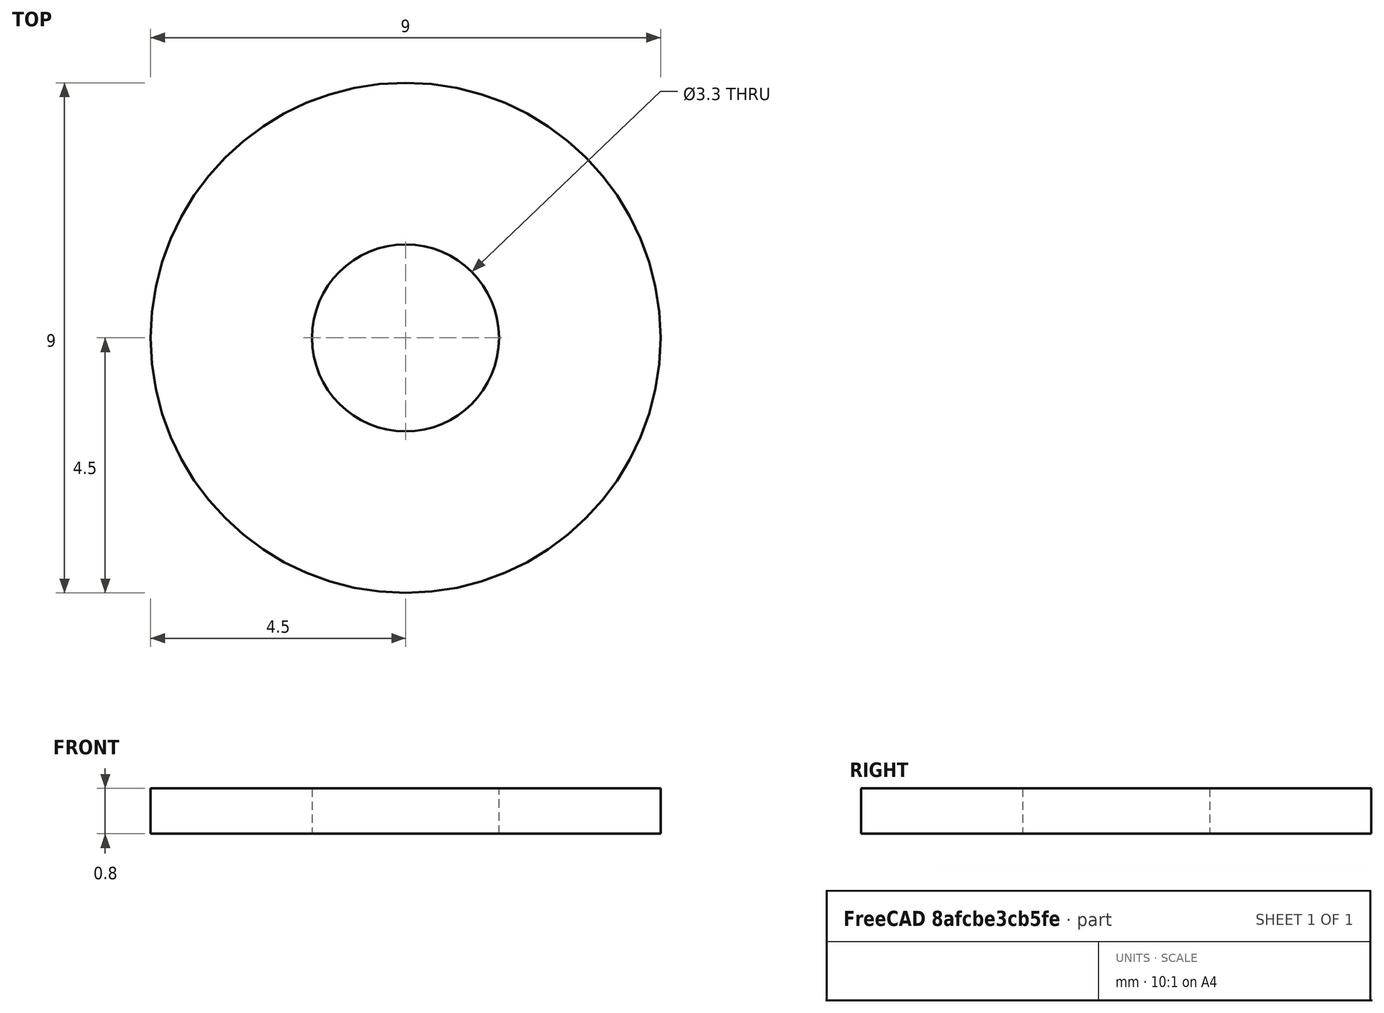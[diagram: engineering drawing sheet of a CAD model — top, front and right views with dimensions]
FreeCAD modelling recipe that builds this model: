
FCSTD DOCUMENT  (FreeCAD 0.17R13519 (Git))
Label: Washer_M3xh0.8xd9
License: All rights reserved
LicenseURL: http://en.wikipedia.org/wiki/All_rights_reserved
objects: Sketcher::SketchObject×1, PartDesign::Pad×1, PartDesign::Body×1
note: 4 computed .brp shape members not serialized (recipe doc carries the construction recipe); baked Part::Feature solids carry a one-line shape summary decoded from their .brp

FEATURE [Sketcher::SketchObject] Sketch
  MapMode = 5
  Support = -> [XY_Plane]
  sketch-geometry (2):
    g0: Circle CenterX=0 CenterY=0 CenterZ=0 NormalX=0 NormalY=0 NormalZ=1 AngleXU=0 Radius=1.65
    g1: Circle CenterX=0 CenterY=0 CenterZ=0 NormalX=0 NormalY=0 NormalZ=1 AngleXU=0 Radius=4.5
  constraints (4):
    c: Coincident(g0,g-1)
    c: Coincident(g1,g-1)
    c: Radius(g0) = 1.65
    c: Radius(g1) = 4.5
FEATURE [PartDesign::Pad] Pad
  Length = 0.8
  Length2 = 100
  Profile = -> Sketch
  Type = 0
FEATURE [PartDesign::Body] Body
  Group = -> [Sketch,Pad]
  Origin = -> Origin
  Tip = -> Pad
